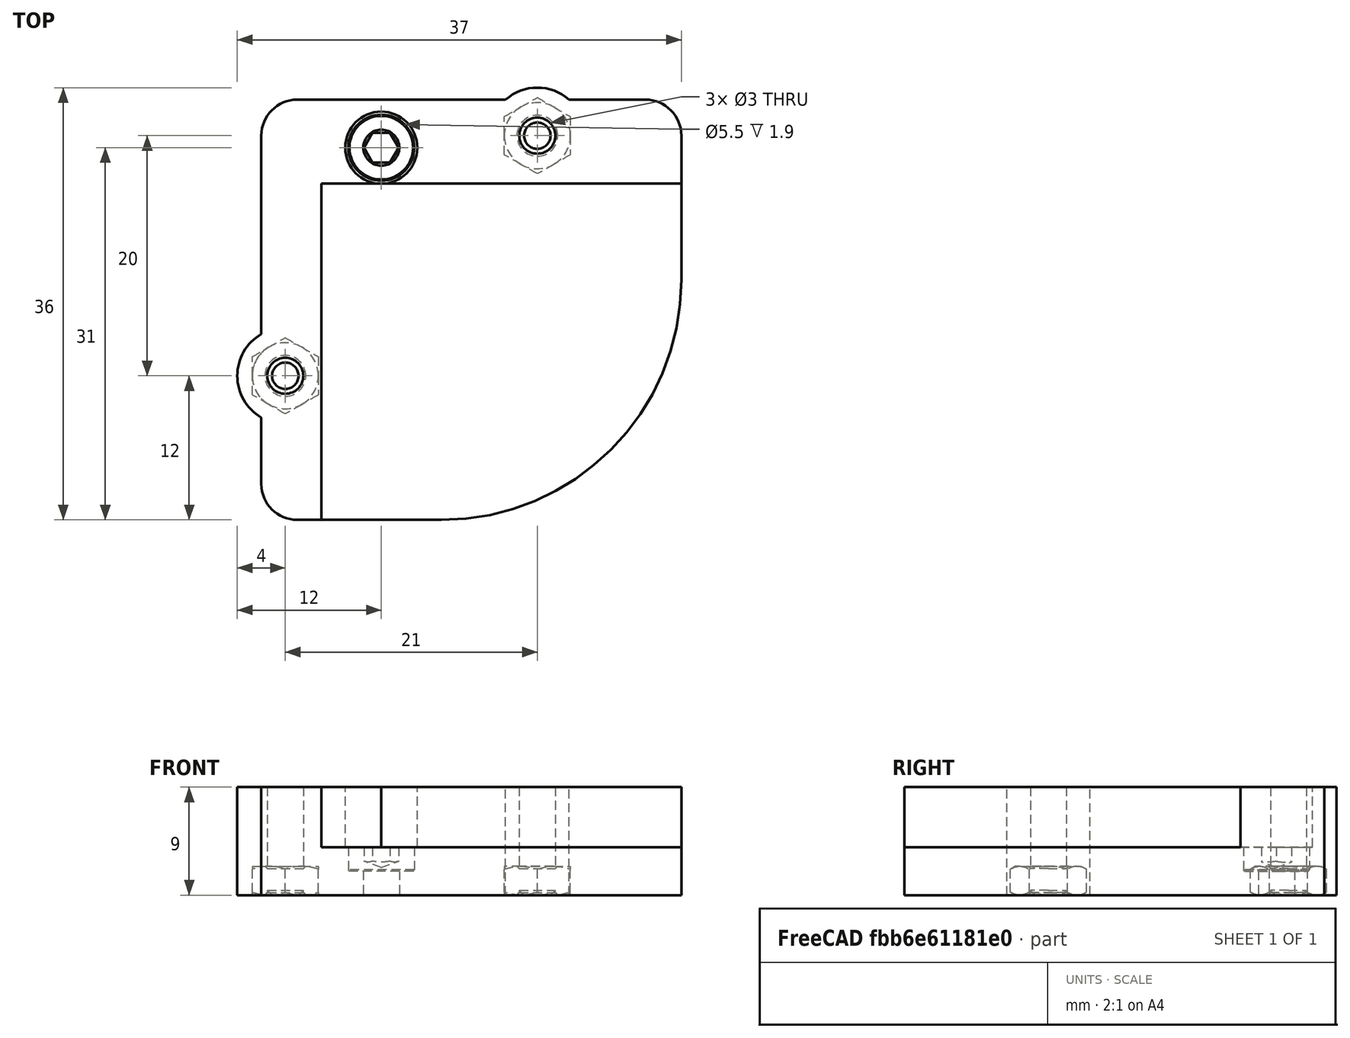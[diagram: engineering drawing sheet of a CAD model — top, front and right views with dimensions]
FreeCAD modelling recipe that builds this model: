
FCSTD DOCUMENT  (FreeCAD 0.14R3702 (Git))
Label: soportes_cama_caliente_v2
License: CC-BY 3.0
LicenseURL: http://creativecommons.org/licenses/by/3.0/
objects: Part::MultiFuse×10, Part::Box×4, Part::Cut×4, Part::Feature×3, Part::Cylinder×3, Part::Fillet×2, Part::Mirroring×1
note: 27 computed .brp shape members not serialized (recipe doc carries the construction recipe); baked Part::Feature solids carry a one-line shape summary decoded from their .brp

FEATURE [Part::Box] Box  label="Cubo"
  Height = 9
  Length = 35
  Width = 35
FEATURE [Part::Feature] Part__Feature  label="Chamfer001"
  shape: bbox 5.5 x 5.5 x 13 mm, 16 faces (baked)
FEATURE [Part::Feature] Part__Feature001  label="Chamfer002"
  shape: bbox 5.5 x 5.5 x 13 mm, 16 faces (baked)
FEATURE [Part::Box] Box001  label="Placa"
  Height = 4
  Length = 90
  Placement = pos=(5,5,4) rot=(0,0,1;0rad)
  Width = 50
FEATURE [Part::Box] Box002  label="Placa001"
  Height = 4
  Length = 90
  Placement = pos=(5,5,6) rot=(0,0,1;0rad)
  Width = 50
FEATURE [Part::MultiFuse] Fusion  label="Placa002"
  Placement = pos=(0,2,0) rot=(0,0,1;0rad)
  Shapes = -> [Box002,Box001]
FEATURE [Part::Cylinder] Cylinder  label="Cilindro"
  Angle = 360
  Height = 5
  Placement = pos=(0,0,2) rot=(0,0,1;0rad)
  Radius = 3
FEATURE [Part::MultiFuse] Fusion001  label="Taladro1"
  Placement = pos=(10,4,2) rot=(0,0,1;0rad)
  Shapes = -> [Cylinder,Part__Feature]
FEATURE [Part::Feature] Part__Feature003  label="Chamfer"
  Placement = pos=(0,0,-10) rot=(0,0,1;0rad)
  shape: bbox 6.35 x 6.35 x 2.4 mm, 29 faces (baked)
FEATURE [Part::Cylinder] Cylinder001  label="Cilindro001"
  Angle = 360
  Height = 9
  Placement = pos=(2,23,0) rot=(0,0,1;0rad)
  Radius = 4
FEATURE [Part::MultiFuse] Fusion002  label="tornillo_tuerca"
  Placement = pos=(2,23,10) rot=(0,0,1;0rad)
  Shapes = -> [Part__Feature001,Part__Feature003]
FEATURE [Part::MultiFuse] Fusion005  label="tornillo_tuerca001"
  Placement = pos=(23,3,10) rot=(0,0,1;0rad)
  Shapes = -> [Part__Feature001,Part__Feature003]
FEATURE [Part::Cylinder] Cylinder002  label="Cilindro002"
  Angle = 360
  Height = 9
  Placement = pos=(23,3,0) rot=(0,0,1;0rad)
  Radius = 4
FEATURE [Part::MultiFuse] Fusion007  label="tornilleria"
  Shapes = -> [Fusion001,Fusion002,Fusion005]
FEATURE [Part::Fillet] Fillet
  Base = -> Box
  Edges = 4 edges: [Edge1 r=3,Edge3 r=3,Edge5 r=3,Edge7 r=20]
FEATURE [Part::MultiFuse] Fusion008  label="Base"
  Shapes = -> [Fillet,Cylinder002,Cylinder001]
FEATURE [Part::Box] Box003  label="Cubo001"
  Height = 1
  Length = 36
  Placement = pos=(-3,22.7,9) rot=(0,0,-1;0.750492rad)
  Width = 7
FEATURE [Part::Fillet] Fillet001
  Base = -> Box003
  Edges = 4 edges r=3: [Edge1,Edge3,Edge5,Edge7]
FEATURE [Part::MultiFuse] Fusion010  label="tornillo_tuerca002"
  Placement = pos=(23,3,10) rot=(0,0,1;0rad)
  Shapes = -> [Part__Feature001,Part__Feature003]
FEATURE [Part::MultiFuse] Fusion011  label="tornillo_tuerca003"
  Placement = pos=(2,23,10) rot=(0,0,1;0rad)
  Shapes = -> [Part__Feature001,Part__Feature003]
FEATURE [Part::MultiFuse] Fusion012  label="Taladro002"
  Placement = pos=(10,4,2) rot=(0,0,1;0rad)
  Shapes = -> [Cylinder,Part__Feature]
FEATURE [Part::MultiFuse] Fusion009  label="tornilleria001"
  Shapes = -> [Fusion012,Fusion011,Fusion010]
FEATURE [Part::Cut] Cut  label="Chapa"
  Base = -> Fillet001
  Tool = -> Fusion009
FEATURE [Part::Cut] Cut001
  Base = -> Fusion008
  Tool = -> Fusion
FEATURE [Part::Cut] Cut002
  Base = -> Cut001
  Tool = -> Cut
FEATURE [Part::Cut] Cut003  label="Pieza"
  Base = -> Cut002
  Tool = -> Fusion007
FEATURE [Part::Mirroring] Part__Mirroring  label="Pieza (Mirror #1)"
  Base = (0,0,0)
  Normal = (0,0,1)
  Placement = pos=(0,-12,0) rot=(1,0,0;3.14159rad)
  Source = -> Cut003
